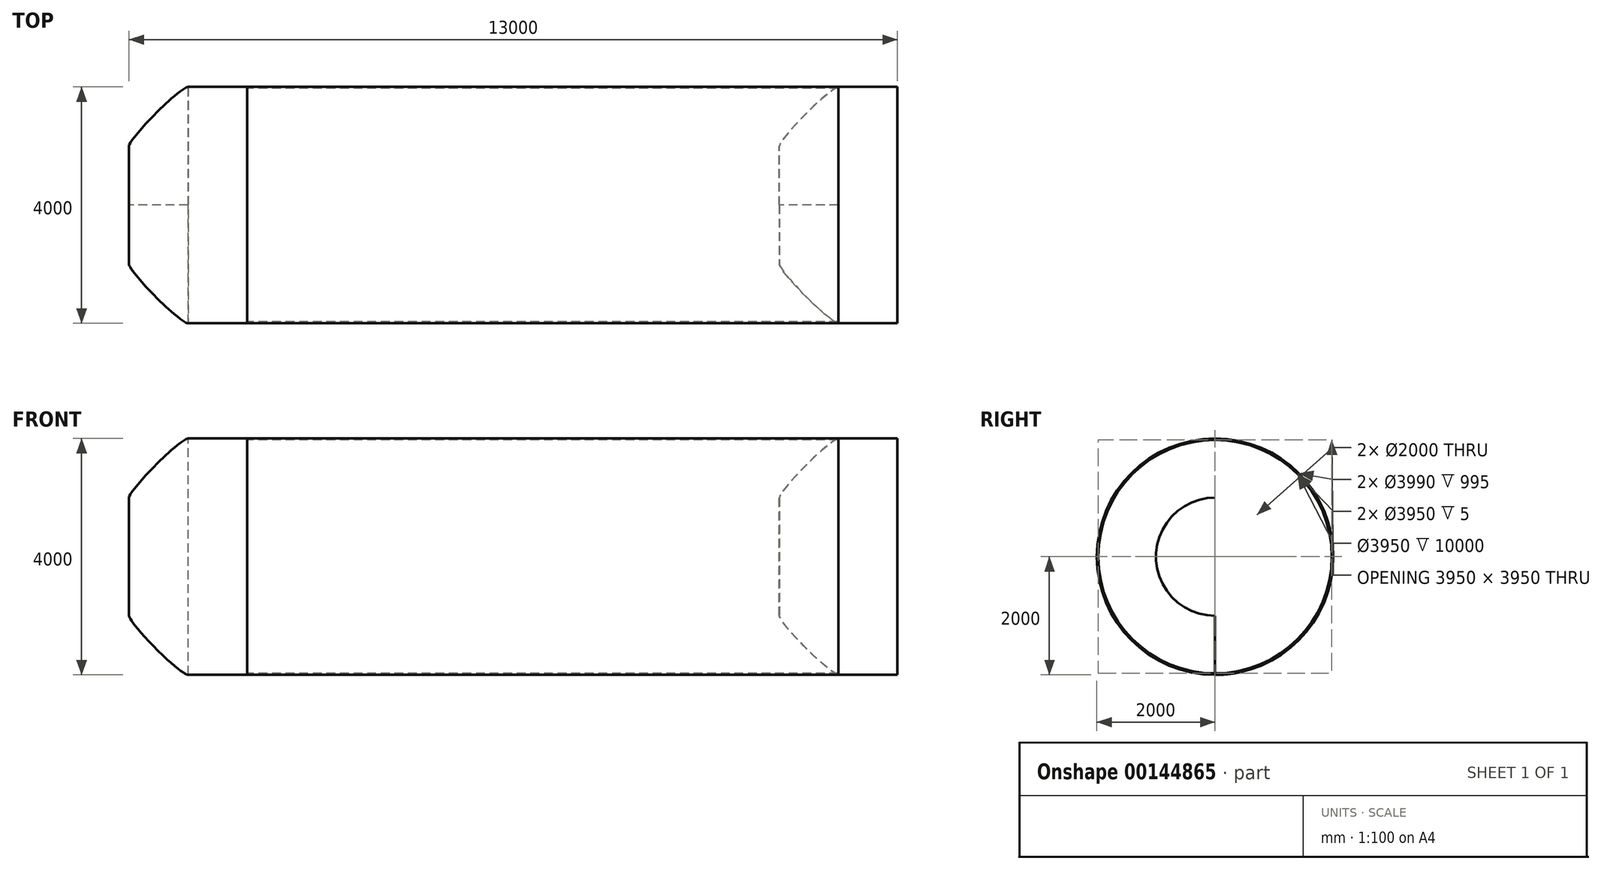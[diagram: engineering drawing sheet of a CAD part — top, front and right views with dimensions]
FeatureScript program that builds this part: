
annotation { "Feature Type Name" : "Feature", "Feature Type Description" : "" }
export const myFeature = defineFeature(function(context is Context, id is Id, definition is map)
    precondition{}
    {
        {
            var Q0;
            Q0=qCreatedBy(makeId("Right.planeOp"),FACE);
            var sketch = newSketch(context, id + "F0", { "sketchPlane" : qUnion([Q0])});
            skCircle(sketch, "E0", {"center": v(0, 0) * mm, "radius": 2000 * mm});
            skCircle(sketch, "E1", {"center": v(0, 0) * mm, "radius": 1975 * mm});
            skSolve(sketch);
        }
        {
            var Q0;
            Q0=makeQuery(id+"F0.imprint","IMPRINT",FACE,{"disambiguationData":[TD([[makeQuery(id+"F0.imprint","IMPRINT",EDGE,{"derivedFrom":sQuery(id+"F0.wireOp",EDGE,"E0")}),1.0]])]});
            extrude(context, id + "F1", {"entities" : qUnion([Q0]), "depth" : 10000 * mm});
        }
        {
            var Q0;
            Q0=qCreatedBy(makeId("Right.planeOp"),FACE);
            cPlane(context, id + "F2", {"entities" : qUnion([Q0]), "cplaneType" : CPlaneType.OFFSET, "offset" : 0 * mm, "width" : 150 * mm, "height" : 150 * mm});
        }
        {
            var Q0;
            Q0=qCreatedBy(id+"F2.planeOp",FACE);
            var sketch = newSketch(context, id + "F3", { "sketchPlane" : qUnion([Q0])});
            skCircle(sketch, "E2", {"center": v(0, 0) * mm, "radius": 2000 * mm});
            skSolve(sketch);
        }
        {
            var Q0;
            Q0 = qSketchRegion(id + "F3", true);
            extrude(context, id + "F4", {"entities" : qUnion([Q0]), "oppositeDirection" : true, "depth" : 2000 * mm});
        }
        {
            var Q0;
            Q0=makeQuery(id+"F4.opExtrude","CAP_EDGE",EDGE,{"disambiguationData":[OSD([sQuery(id+"F3.wireOp",EDGE,"E2")])],"isStart":false});
            fillet(context, id + "F5", {"entities" : qUnion([Q0]), "radius" : 1000 * mm, "tangentPropagation" : true, "rho" : 0.1, "crossSection" : FilletCrossSection.CONIC, "allowEdgeOverflow" : false});
        }
        {
            var Q0;
            Q0=makeQuery(id+"F4.opExtrude","CAP_FACE",FACE,{"disambiguationData":[OSD([sQuery(id+"F3.wireOp",EDGE,"E2")])],"isStart":false});
            shell(context, id + "F6", {"entities" : qUnion([Q0]), "thickness" : 5 * mm});
        }
        {
            var Q0;
            {var subQ0=sQuery(id+"F3.wireOp",EDGE,"E2");Q0=makeQuery(id+"F6.opShell","OFFSET_FACE",FACE,{"disambiguationData":[OSD([subQ0]),TDD([makeQuery(id+"F4.opExtrude","CAP_FACE",FACE,{"disambiguationData":[OSD([subQ0])],"isStart":true})])]});}
            var sketch = newSketch(context, id + "F7", { "sketchPlane" : qUnion([Q0])});
            skCircle(sketch, "E3", {"center": v(0, 0) * mm, "radius": 975 * mm});
            skSolve(sketch);
        }
        {
            var Q0;
            Q0=sQuery(id+"F7.wireOp",VERTEX,"E3.center");
            var Q1;
            Q1=makeQuery(id+"F4.opExtrude","SWEPT_BODY",BODY,{"disambiguationData":[OSD([sQuery(id+"F3.wireOp",EDGE,"E2")])]});
            hole(context, id + "F8", {"style" : HoleStyle.SIMPLE, "endStyle" : HoleEndStyle.THROUGH, "holeDiameter" : 3950 * mm, "locations" : qUnion([Q0]), "scope" : qUnion([Q1]), "isTappedThrough" : true});
        }
        {
            var Q0;
            Q0=makeQuery(id+"F4.opExtrude","SWEPT_BODY",BODY,{"disambiguationData":[OSD([sQuery(id+"F3.wireOp",EDGE,"E2")])]});
            transform(context, id + "F9", {"entities" : qUnion([Q0]), "transformType" : TransformType.TRANSLATION_3D, "dx" : 11000 * mm, "dy" : 0 * mm, "dz" : 0 * mm, "makeCopy" : true});
        }
    });
